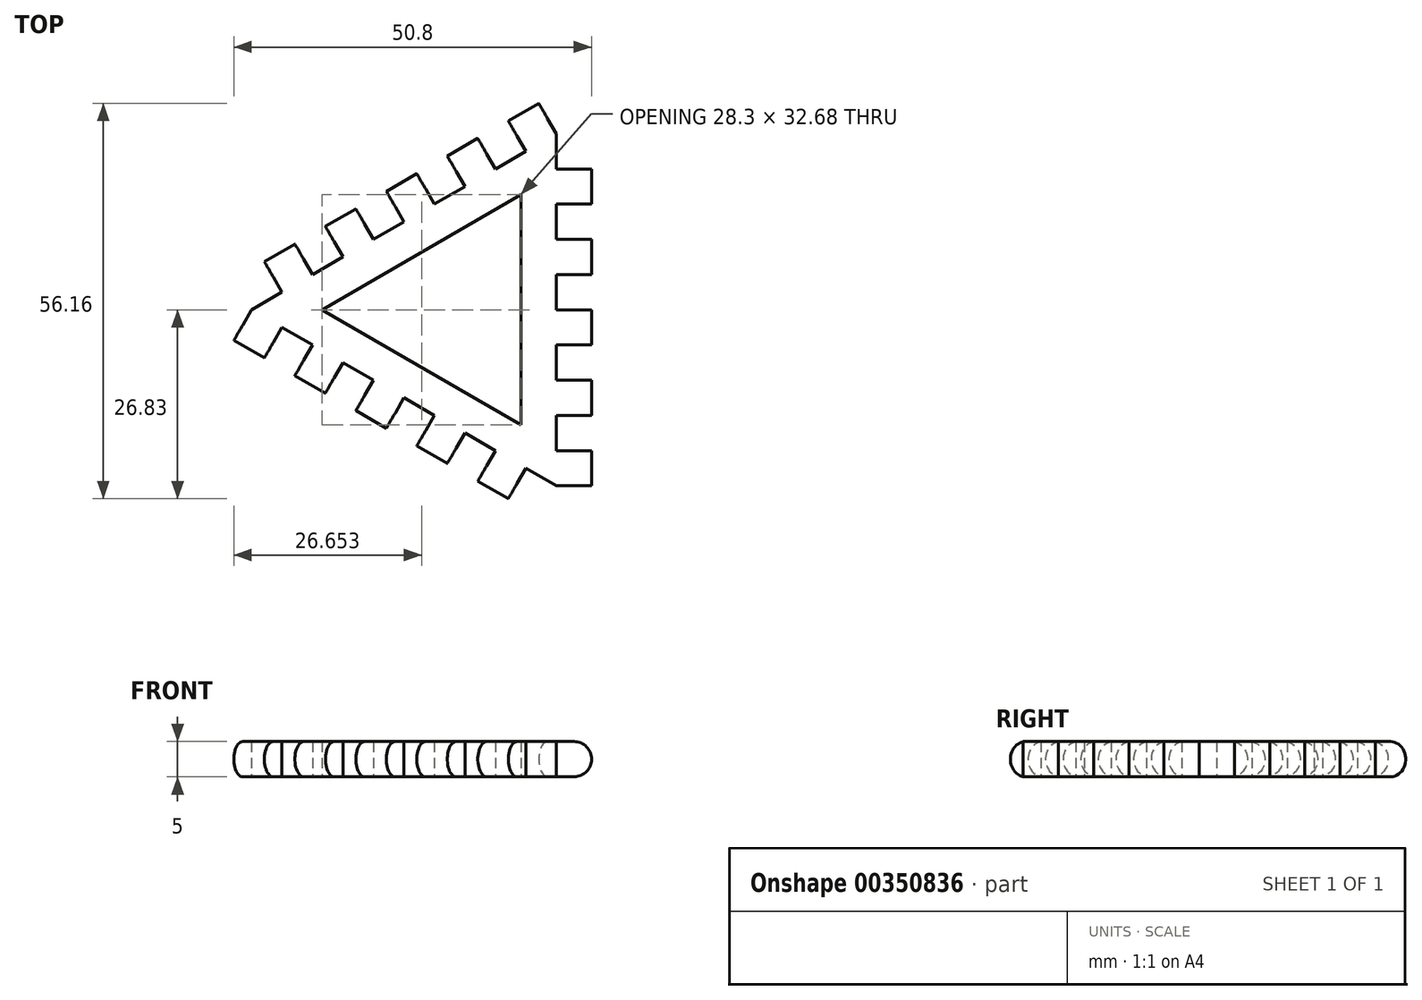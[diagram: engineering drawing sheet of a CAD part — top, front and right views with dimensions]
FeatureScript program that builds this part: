
annotation { "Feature Type Name" : "Feature", "Feature Type Description" : "" }
export const myFeature = defineFeature(function(context is Context, id is Id, definition is map)
    precondition{}
    {
        {
            var Q0;
            Q0=qCreatedBy(makeId("Top.planeOp"),FACE);
            var sketch = newSketch(context, id + "F0", { "sketchPlane" : qUnion([Q0])});
            skCircle(sketch, "E0.cCircle", {"center": v(0, 0) * mm, "radius": 14.43 * mm, "construction": true});
            skLineSegment(sketch, "E0.0", {"start": v(14.43, 25) * mm, "end": v(14.43, -25) * mm});
            skLineSegment(sketch, "E0.1", {"start": v(14.43, -25) * mm, "end": v(-28.87, 0) * mm});
            skLineSegment(sketch, "E0.2", {"start": v(-28.87, 0) * mm, "end": v(14.43, 25) * mm});
            skPoint(sketch, "E0.0.midPoint", {"position": v(14.43, 0) * mm});
            skLineSegment(sketch, "E1.bottom", {"start": v(14.43, -25) * mm, "end": v(19.43, -25) * mm});
            skLineSegment(sketch, "E1.top", {"start": v(14.43, -20) * mm, "end": v(19.43, -20) * mm});
            skLineSegment(sketch, "E1.left", {"start": v(14.43, -25) * mm, "end": v(14.43, -20) * mm});
            skLineSegment(sketch, "E1.right", {"start": v(19.43, -25) * mm, "end": v(19.43, -20) * mm});
            skLineSegment(sketch, "E2.0.1.0", {"start": v(14.43, -15) * mm, "end": v(14.43, -10) * mm});
            skLineSegment(sketch, "E2.0.1.1", {"start": v(14.43, -10) * mm, "end": v(19.43, -10) * mm});
            skLineSegment(sketch, "E2.0.1.2", {"start": v(19.43, -15) * mm, "end": v(19.43, -10) * mm});
            skLineSegment(sketch, "E2.0.1.3", {"start": v(14.43, -15) * mm, "end": v(19.43, -15) * mm});
            skLineSegment(sketch, "E2.0.2.0", {"start": v(14.43, -5) * mm, "end": v(14.43, 0) * mm});
            skLineSegment(sketch, "E2.0.2.1", {"start": v(14.43, 0) * mm, "end": v(19.43, 0) * mm});
            skLineSegment(sketch, "E2.0.2.2", {"start": v(19.43, -5) * mm, "end": v(19.43, 0) * mm});
            skLineSegment(sketch, "E2.0.2.3", {"start": v(14.43, -5) * mm, "end": v(19.43, -5) * mm});
            skLineSegment(sketch, "E2.0.3.0", {"start": v(14.43, 5) * mm, "end": v(14.43, 10) * mm});
            skLineSegment(sketch, "E2.0.3.1", {"start": v(14.43, 10) * mm, "end": v(19.43, 10) * mm});
            skLineSegment(sketch, "E2.0.3.2", {"start": v(19.43, 5) * mm, "end": v(19.43, 10) * mm});
            skLineSegment(sketch, "E2.0.3.3", {"start": v(14.43, 5) * mm, "end": v(19.43, 5) * mm});
            skLineSegment(sketch, "E2.0.4.0", {"start": v(14.43, 15) * mm, "end": v(14.43, 20) * mm});
            skLineSegment(sketch, "E2.0.4.1", {"start": v(14.43, 20) * mm, "end": v(19.43, 20) * mm});
            skLineSegment(sketch, "E2.0.4.2", {"start": v(19.43, 15) * mm, "end": v(19.43, 20) * mm});
            skLineSegment(sketch, "E2.0.4.3", {"start": v(14.43, 15) * mm, "end": v(19.43, 15) * mm});
            skLineSegment(sketch, "E3.1.0", {"start": v(14.43, 25) * mm, "end": v(10.1, 22.5) * mm});
            skLineSegment(sketch, "E3.1.1", {"start": v(14.43, 25) * mm, "end": v(11.93, 29.33) * mm});
            skLineSegment(sketch, "E3.1.2", {"start": v(11.93, 29.33) * mm, "end": v(7.6, 26.83) * mm});
            skLineSegment(sketch, "E3.1.3", {"start": v(10.1, 22.5) * mm, "end": v(7.6, 26.83) * mm});
            skLineSegment(sketch, "E3.1.4", {"start": v(5.77, 20) * mm, "end": v(1.44, 17.5) * mm});
            skLineSegment(sketch, "E3.1.5", {"start": v(5.77, 20) * mm, "end": v(3.27, 24.33) * mm});
            skLineSegment(sketch, "E3.1.6", {"start": v(3.27, 24.33) * mm, "end": v(-1.06, 21.83) * mm});
            skLineSegment(sketch, "E3.1.7", {"start": v(1.44, 17.5) * mm, "end": v(-1.06, 21.83) * mm});
            skLineSegment(sketch, "E3.1.8", {"start": v(-2.89, 15) * mm, "end": v(-7.22, 12.5) * mm});
            skLineSegment(sketch, "E3.1.9", {"start": v(-2.89, 15) * mm, "end": v(-5.39, 19.33) * mm});
            skLineSegment(sketch, "E3.1.10", {"start": v(-5.39, 19.33) * mm, "end": v(-9.72, 16.83) * mm});
            skLineSegment(sketch, "E3.1.11", {"start": v(-7.22, 12.5) * mm, "end": v(-9.72, 16.83) * mm});
            skLineSegment(sketch, "E3.1.12", {"start": v(-11.55, 10) * mm, "end": v(-15.88, 7.5) * mm});
            skLineSegment(sketch, "E3.1.13", {"start": v(-11.55, 10) * mm, "end": v(-14.05, 14.33) * mm});
            skLineSegment(sketch, "E3.1.14", {"start": v(-14.05, 14.33) * mm, "end": v(-18.38, 11.83) * mm});
            skLineSegment(sketch, "E3.1.15", {"start": v(-15.88, 7.5) * mm, "end": v(-18.38, 11.83) * mm});
            skLineSegment(sketch, "E3.1.16", {"start": v(-20.2, 5) * mm, "end": v(-24.54, 2.5) * mm});
            skLineSegment(sketch, "E3.1.17", {"start": v(-20.2, 5) * mm, "end": v(-22.7, 9.33) * mm});
            skLineSegment(sketch, "E3.1.18", {"start": v(-22.7, 9.33) * mm, "end": v(-27.04, 6.83) * mm});
            skLineSegment(sketch, "E3.1.19", {"start": v(-24.54, 2.5) * mm, "end": v(-27.04, 6.83) * mm});
            skLineSegment(sketch, "E3.2.0", {"start": v(-28.87, 0) * mm, "end": v(-24.54, -2.5) * mm});
            skLineSegment(sketch, "E3.2.1", {"start": v(-28.87, 0) * mm, "end": v(-31.37, -4.33) * mm});
            skLineSegment(sketch, "E3.2.2", {"start": v(-31.37, -4.33) * mm, "end": v(-27.04, -6.83) * mm});
            skLineSegment(sketch, "E3.2.3", {"start": v(-24.54, -2.5) * mm, "end": v(-27.04, -6.83) * mm});
            skLineSegment(sketch, "E3.2.4", {"start": v(-20.2, -5) * mm, "end": v(-15.88, -7.5) * mm});
            skLineSegment(sketch, "E3.2.5", {"start": v(-20.2, -5) * mm, "end": v(-22.7, -9.33) * mm});
            skLineSegment(sketch, "E3.2.6", {"start": v(-22.7, -9.33) * mm, "end": v(-18.38, -11.83) * mm});
            skLineSegment(sketch, "E3.2.7", {"start": v(-15.88, -7.5) * mm, "end": v(-18.38, -11.83) * mm});
            skLineSegment(sketch, "E3.2.8", {"start": v(-11.55, -10) * mm, "end": v(-7.22, -12.5) * mm});
            skLineSegment(sketch, "E3.2.9", {"start": v(-11.55, -10) * mm, "end": v(-14.05, -14.33) * mm});
            skLineSegment(sketch, "E3.2.10", {"start": v(-14.05, -14.33) * mm, "end": v(-9.72, -16.83) * mm});
            skLineSegment(sketch, "E3.2.11", {"start": v(-7.22, -12.5) * mm, "end": v(-9.72, -16.83) * mm});
            skLineSegment(sketch, "E3.2.12", {"start": v(-2.89, -15) * mm, "end": v(1.44, -17.5) * mm});
            skLineSegment(sketch, "E3.2.13", {"start": v(-2.89, -15) * mm, "end": v(-5.39, -19.33) * mm});
            skLineSegment(sketch, "E3.2.14", {"start": v(-5.39, -19.33) * mm, "end": v(-1.06, -21.83) * mm});
            skLineSegment(sketch, "E3.2.15", {"start": v(1.44, -17.5) * mm, "end": v(-1.06, -21.83) * mm});
            skLineSegment(sketch, "E3.2.16", {"start": v(5.77, -20) * mm, "end": v(10.1, -22.5) * mm});
            skLineSegment(sketch, "E3.2.17", {"start": v(5.77, -20) * mm, "end": v(3.27, -24.33) * mm});
            skLineSegment(sketch, "E3.2.18", {"start": v(3.27, -24.33) * mm, "end": v(7.6, -26.83) * mm});
            skLineSegment(sketch, "E3.2.19", {"start": v(10.1, -22.5) * mm, "end": v(7.6, -26.83) * mm});
            skLineSegment(sketch, "E4.0", {"start": v(-18.87, 0) * mm, "end": v(9.43, 16.34) * mm});
            skLineSegment(sketch, "E4.1", {"start": v(9.43, -16.34) * mm, "end": v(-18.87, 0) * mm});
            skLineSegment(sketch, "E4.2", {"start": v(9.43, 16.34) * mm, "end": v(9.43, -16.34) * mm});
            skSolve(sketch);
        }
        {
            var Q0;
            Q0 = qSketchRegion(id + "F0", true);
            extrude(context, id + "F1", {"entities" : qUnion([Q0]), "depth" : 5 * mm});
        }
        {
            var Q0;
            Q0=makeQuery(id+"F1.opExtrude","CAP_EDGE",EDGE,{"disambiguationData":[OSD([sQuery(id+"F0.wireOp",EDGE,"E3.2.2")])],"isStart":false});
            var Q1;
            Q1=makeQuery(id+"F1.opExtrude","CAP_EDGE",EDGE,{"disambiguationData":[OSD([sQuery(id+"F0.wireOp",EDGE,"E3.2.6")])],"isStart":false});
            var Q2;
            Q2=makeQuery(id+"F1.opExtrude","CAP_EDGE",EDGE,{"disambiguationData":[OSD([sQuery(id+"F0.wireOp",EDGE,"E3.2.10")])],"isStart":false});
            var Q3;
            Q3=makeQuery(id+"F1.opExtrude","CAP_EDGE",EDGE,{"disambiguationData":[OSD([sQuery(id+"F0.wireOp",EDGE,"E3.2.14")])],"isStart":false});
            var Q4;
            Q4=makeQuery(id+"F1.opExtrude","CAP_EDGE",EDGE,{"disambiguationData":[OSD([sQuery(id+"F0.wireOp",EDGE,"E3.2.18")])],"isStart":false});
            var Q5;
            Q5=makeQuery(id+"F1.opExtrude","CAP_EDGE",EDGE,{"disambiguationData":[OSD([sQuery(id+"F0.wireOp",EDGE,"E1.right")])],"isStart":false});
            var Q6;
            Q6=makeQuery(id+"F1.opExtrude","CAP_EDGE",EDGE,{"disambiguationData":[OSD([sQuery(id+"F0.wireOp",EDGE,"E2.0.1.2")])],"isStart":false});
            var Q7;
            Q7=makeQuery(id+"F1.opExtrude","CAP_EDGE",EDGE,{"disambiguationData":[OSD([sQuery(id+"F0.wireOp",EDGE,"E2.0.2.2")])],"isStart":false});
            var Q8;
            Q8=makeQuery(id+"F1.opExtrude","CAP_EDGE",EDGE,{"disambiguationData":[OSD([sQuery(id+"F0.wireOp",EDGE,"E2.0.3.2")])],"isStart":false});
            var Q9;
            Q9=makeQuery(id+"F1.opExtrude","CAP_EDGE",EDGE,{"disambiguationData":[OSD([sQuery(id+"F0.wireOp",EDGE,"E2.0.4.2")])],"isStart":false});
            var Q10;
            Q10=makeQuery(id+"F1.opExtrude","CAP_EDGE",EDGE,{"disambiguationData":[OSD([sQuery(id+"F0.wireOp",EDGE,"E3.1.2")])],"isStart":false});
            var Q11;
            Q11=makeQuery(id+"F1.opExtrude","CAP_EDGE",EDGE,{"disambiguationData":[OSD([sQuery(id+"F0.wireOp",EDGE,"E3.1.6")])],"isStart":false});
            var Q12;
            Q12=makeQuery(id+"F1.opExtrude","CAP_EDGE",EDGE,{"disambiguationData":[OSD([sQuery(id+"F0.wireOp",EDGE,"E3.1.10")])],"isStart":false});
            var Q13;
            Q13=makeQuery(id+"F1.opExtrude","CAP_EDGE",EDGE,{"disambiguationData":[OSD([sQuery(id+"F0.wireOp",EDGE,"E3.1.14")])],"isStart":false});
            var Q14;
            Q14=makeQuery(id+"F1.opExtrude","CAP_EDGE",EDGE,{"disambiguationData":[OSD([sQuery(id+"F0.wireOp",EDGE,"E3.1.18")])],"isStart":false});
            var Q15;
            Q15=makeQuery(id+"F1.opExtrude","CAP_EDGE",EDGE,{"disambiguationData":[OSD([sQuery(id+"F0.wireOp",EDGE,"E3.2.18")])],"isStart":true});
            var Q16;
            Q16=makeQuery(id+"F1.opExtrude","CAP_EDGE",EDGE,{"disambiguationData":[OSD([sQuery(id+"F0.wireOp",EDGE,"E3.2.14")])],"isStart":true});
            var Q17;
            Q17=makeQuery(id+"F1.opExtrude","CAP_EDGE",EDGE,{"disambiguationData":[OSD([sQuery(id+"F0.wireOp",EDGE,"E3.2.10")])],"isStart":true});
            var Q18;
            Q18=makeQuery(id+"F1.opExtrude","CAP_EDGE",EDGE,{"disambiguationData":[OSD([sQuery(id+"F0.wireOp",EDGE,"E3.2.6")])],"isStart":true});
            var Q19;
            Q19=makeQuery(id+"F1.opExtrude","CAP_EDGE",EDGE,{"disambiguationData":[OSD([sQuery(id+"F0.wireOp",EDGE,"E3.2.2")])],"isStart":true});
            var Q20;
            Q20=makeQuery(id+"F1.opExtrude","CAP_EDGE",EDGE,{"disambiguationData":[OSD([sQuery(id+"F0.wireOp",EDGE,"E3.1.18")])],"isStart":true});
            var Q21;
            Q21=makeQuery(id+"F1.opExtrude","CAP_EDGE",EDGE,{"disambiguationData":[OSD([sQuery(id+"F0.wireOp",EDGE,"E3.1.14")])],"isStart":true});
            var Q22;
            Q22=makeQuery(id+"F1.opExtrude","CAP_EDGE",EDGE,{"disambiguationData":[OSD([sQuery(id+"F0.wireOp",EDGE,"E3.1.10")])],"isStart":true});
            var Q23;
            Q23=makeQuery(id+"F1.opExtrude","CAP_EDGE",EDGE,{"disambiguationData":[OSD([sQuery(id+"F0.wireOp",EDGE,"E3.1.6")])],"isStart":true});
            var Q24;
            Q24=makeQuery(id+"F1.opExtrude","CAP_EDGE",EDGE,{"disambiguationData":[OSD([sQuery(id+"F0.wireOp",EDGE,"E3.1.2")])],"isStart":true});
            var Q25;
            Q25=makeQuery(id+"F1.opExtrude","CAP_EDGE",EDGE,{"disambiguationData":[OSD([sQuery(id+"F0.wireOp",EDGE,"E2.0.4.2")])],"isStart":true});
            var Q26;
            Q26=makeQuery(id+"F1.opExtrude","CAP_EDGE",EDGE,{"disambiguationData":[OSD([sQuery(id+"F0.wireOp",EDGE,"E2.0.3.2")])],"isStart":true});
            var Q27;
            Q27=makeQuery(id+"F1.opExtrude","CAP_EDGE",EDGE,{"disambiguationData":[OSD([sQuery(id+"F0.wireOp",EDGE,"E2.0.2.2")])],"isStart":true});
            var Q28;
            Q28=makeQuery(id+"F1.opExtrude","CAP_EDGE",EDGE,{"disambiguationData":[OSD([sQuery(id+"F0.wireOp",EDGE,"E2.0.1.2")])],"isStart":true});
            var Q29;
            Q29=makeQuery(id+"F1.opExtrude","CAP_EDGE",EDGE,{"disambiguationData":[OSD([sQuery(id+"F0.wireOp",EDGE,"E1.right")])],"isStart":true});
            fillet(context, id + "F2", {"entities" : qUnion([Q0, Q1, Q2, Q3, Q4, Q5, Q6, Q7, Q8, Q9, Q10, Q11, Q12, Q13, Q14, Q15, Q16, Q17, Q18, Q19, Q20, Q21, Q22, Q23, Q24, Q25, Q26, Q27, Q28, Q29]), "radius" : 2.5 * mm, "tangentPropagation" : true, "allowEdgeOverflow" : false});
        }
    });
